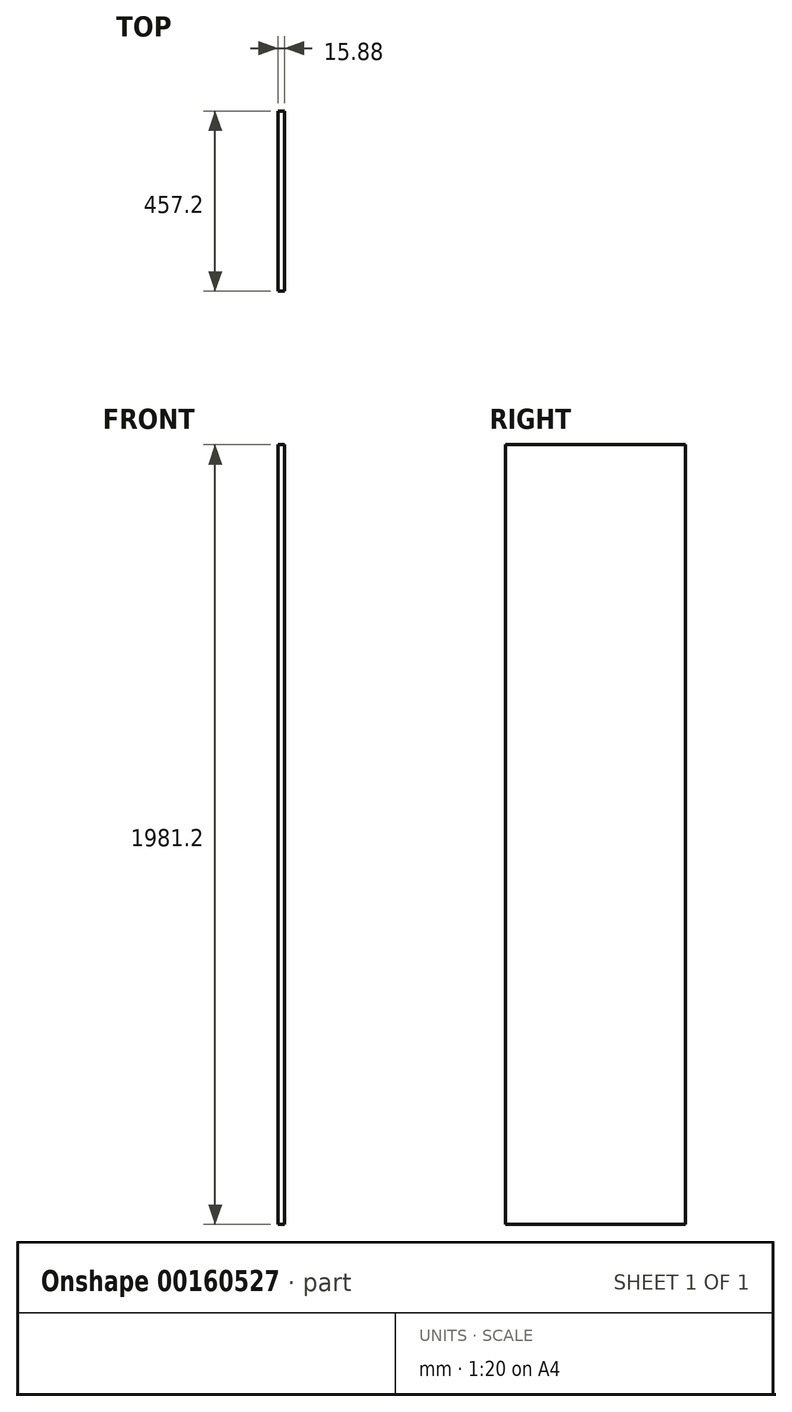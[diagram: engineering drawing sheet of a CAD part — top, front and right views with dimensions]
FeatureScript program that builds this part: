
annotation { "Feature Type Name" : "Feature", "Feature Type Description" : "" }
export const myFeature = defineFeature(function(context is Context, id is Id, definition is map)
    precondition{}
    {
        {
            var Q0;
            Q0=qCreatedBy(makeId("Front.planeOp"),FACE);
            var sketch = newSketch(context, id + "F0", { "sketchPlane" : qUnion([Q0])});
            skLineSegment(sketch, "E0.bottom", {"start": v(0, 0) * mm, "end": v(15.88, 0) * mm});
            skLineSegment(sketch, "E0.top", {"start": v(0, 1981.2) * mm, "end": v(15.87, 1981.2) * mm});
            skLineSegment(sketch, "E0.left", {"start": v(0, 0) * mm, "end": v(0, 1981.2) * mm});
            skLineSegment(sketch, "E0.right", {"start": v(15.88, 0) * mm, "end": v(15.87, 1981.2) * mm});
            skSolve(sketch);
        }
        {
            var Q0;
            Q0=makeQuery(id+"F0.imprint","IMPRINT",FACE,{"disambiguationData":[TD([[makeQuery(id+"F0.imprint","IMPRINT",EDGE,{"derivedFrom":sQuery(id+"F0.wireOp",EDGE,"E0.bottom")}),1.0]])]});
            extrude(context, id + "F1", {"entities" : qUnion([Q0]), "depth" : 457.2 * mm});
        }
    });
